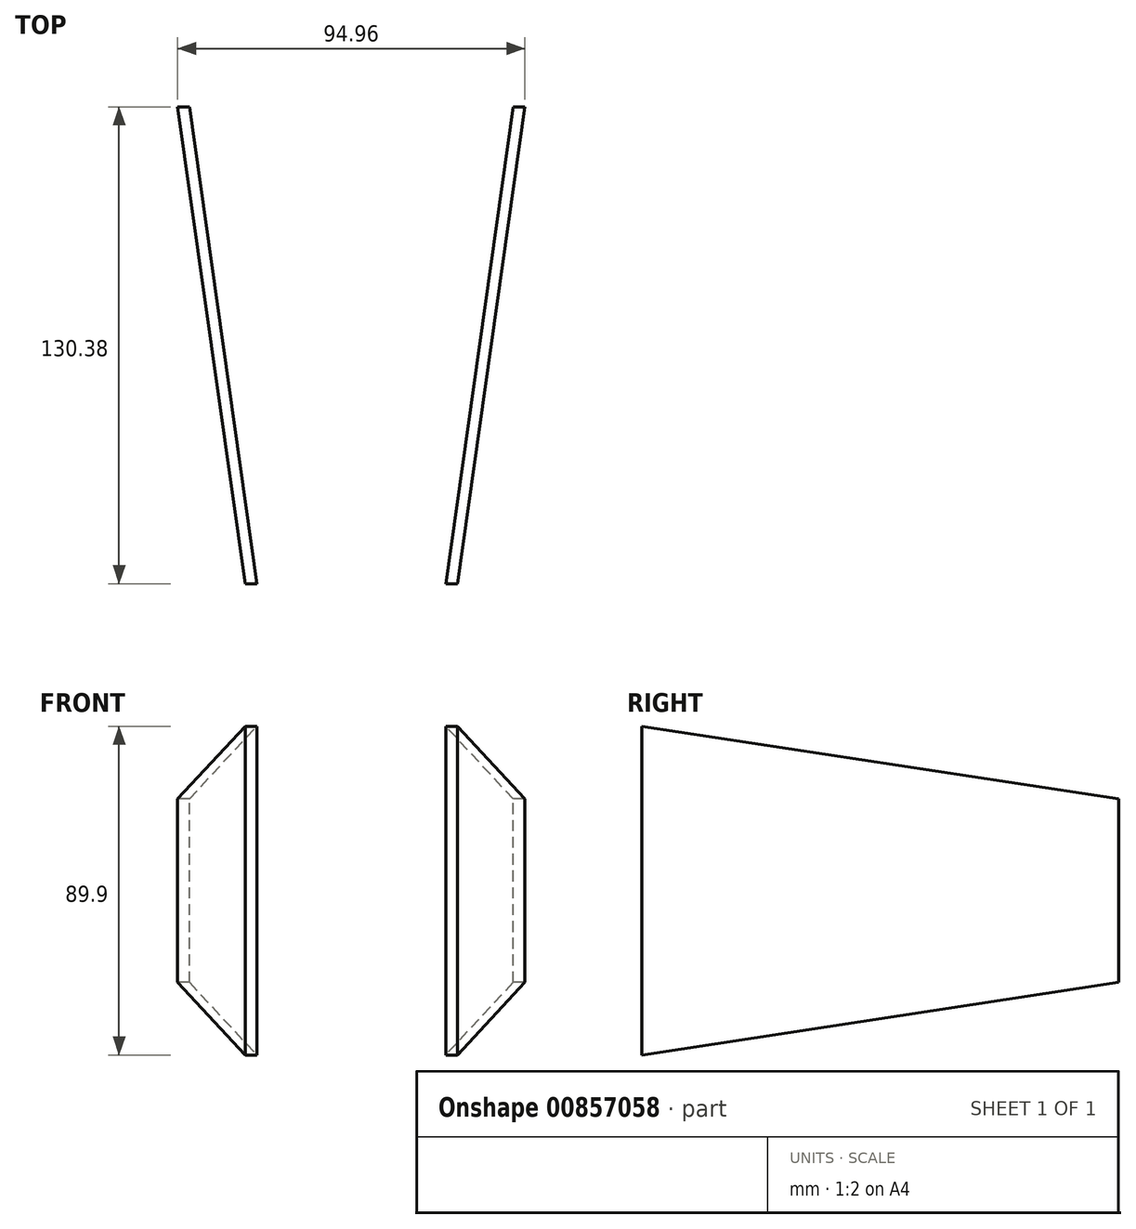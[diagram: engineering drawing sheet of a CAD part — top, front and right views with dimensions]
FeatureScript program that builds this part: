
annotation { "Feature Type Name" : "Feature", "Feature Type Description" : "" }
export const myFeature = defineFeature(function(context is Context, id is Id, definition is map)
    precondition{}
    {
        {
            var Q0;
            Q0=qCreatedBy(makeId("Right.planeOp"),FACE);
            var sketch = newSketch(context, id + "F0", { "sketchPlane" : qUnion([Q0])});
            skLineSegment(sketch, "E0", {"start": v(0, 48.82) * mm, "end": v(0, -48.82) * mm});
            skLineSegment(sketch, "E1", {"start": v(25.4, 44.95) * mm, "end": v(25.4, -44.95) * mm});
            skLineSegment(sketch, "E2", {"start": v(155.78, 25.1) * mm, "end": v(155.78, -25.1) * mm});
            skCircle(sketch, "E3", {"center": v(311.35, 0) * mm, "radius": 1.39 * mm});
            skLineSegment(sketch, "E4", {"start": v(0, 48.82) * mm, "end": v(311.56, 1.37) * mm});
            skLineSegment(sketch, "E5", {"start": v(0, -48.82) * mm, "end": v(311.56, -1.37) * mm});
            skSolve(sketch);
        }
        {
            var Q0;
            {var subQ5=sQuery(id+"F0.wireOp",EDGE,"E2");Q0=makeQuery(id+"F0.imprint","IMPRINT",FACE,{"disambiguationData":[TD([[makeQuery(id+"F0.imprint","IMPRINT",EDGE,{"derivedFrom":subQ5}),-1.0]])]});}
            extrude(context, id + "F1", {"entities" : qUnion([Q0]), "depth" : 254 * mm, "offsetDistance" : 25.4 * mm, "symmetric" : true});
        }
        {
            var Q0;
            Q0=qCreatedBy(makeId("Top.planeOp"),FACE);
            var sketch = newSketch(context, id + "F2", { "sketchPlane" : qUnion([Q0])});
            skLineSegment(sketch, "E6", {"start": v(-66.68, 291.34) * mm, "end": v(66.68, 291.34) * mm});
            skLineSegment(sketch, "E7", {"start": v(0, 0) * mm, "end": v(0, 291.34) * mm});
            skLineSegment(sketch, "E8", {"start": v(-22.23, 0) * mm, "end": v(22.23, 0) * mm});
            skLineSegment(sketch, "E9", {"start": v(-22.22, 0) * mm, "end": v(-63.47, 291.34) * mm});
            skLineSegment(sketch, "E10", {"start": v(-66.67, 291.34) * mm, "end": v(-25.43, 0) * mm});
            skLineSegment(sketch, "E11", {"start": v(-25.43, 0) * mm, "end": v(-22.23, 0) * mm});
            skLineSegment(sketch, "E12", {"start": v(22.22, 0) * mm, "end": v(63.47, 291.34) * mm});
            skLineSegment(sketch, "E13", {"start": v(66.68, 291.34) * mm, "end": v(25.43, 0) * mm});
            skLineSegment(sketch, "E14", {"start": v(25.43, 0) * mm, "end": v(22.23, 0) * mm});
            skSolve(sketch);
        }
        {
            var Q0;
            {var subQ2=sQuery(id+"F2.wireOp",EDGE,"E9");Q0=makeQuery(id+"F2.imprint","IMPRINT",FACE,{"disambiguationData":[TD([[makeQuery(id+"F2.imprint","IMPRINT",EDGE,{"derivedFrom":subQ2}),1.0]])]});}
            var Q1;
            {var subQ2=sQuery(id+"F2.wireOp",EDGE,"E12");Q1=makeQuery(id+"F2.imprint","IMPRINT",FACE,{"disambiguationData":[TD([[makeQuery(id+"F2.imprint","IMPRINT",EDGE,{"derivedFrom":subQ2}),-1.0]])]});}
            extrude(context, id + "F3", {"entities" : qUnion([Q0, Q1]), "operationType" : NewBodyOperationType.INTERSECT, "depth" : 101.6 * mm, "offsetDistance" : 25.4 * mm, "symmetric" : true});
        }
    });
